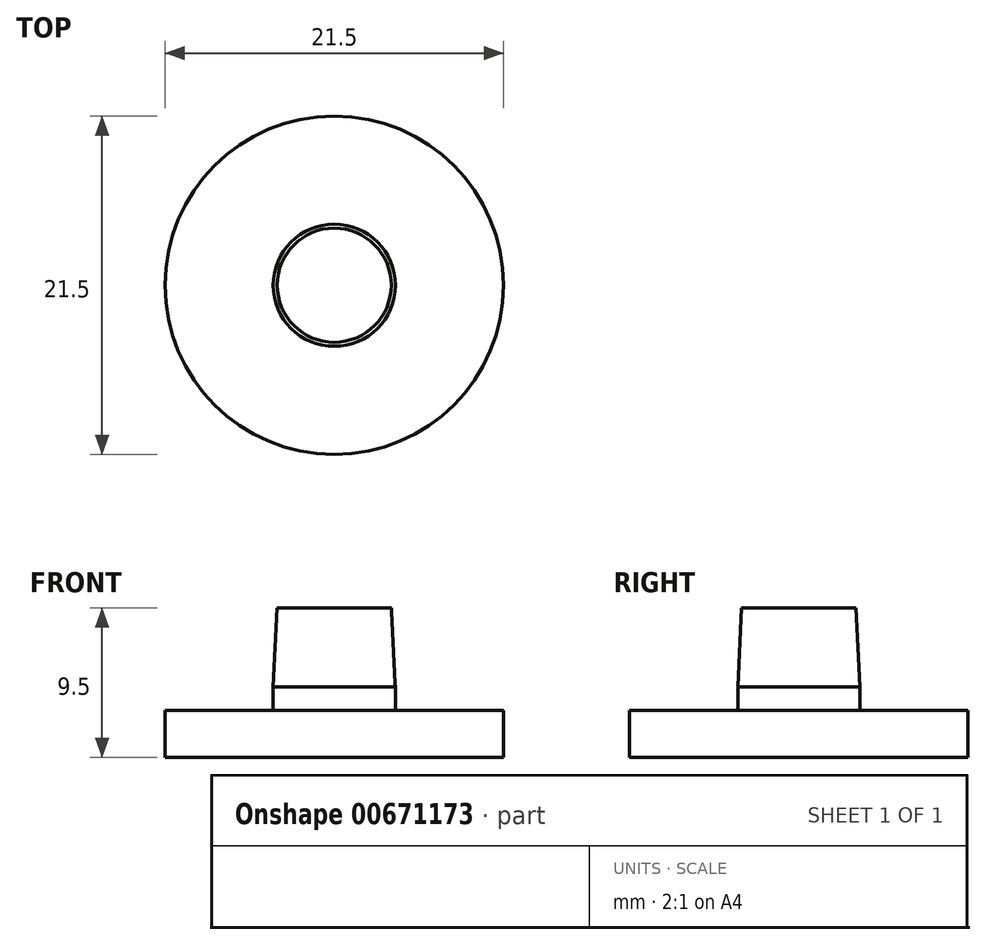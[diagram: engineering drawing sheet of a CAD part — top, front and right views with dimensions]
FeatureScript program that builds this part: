
annotation { "Feature Type Name" : "Feature", "Feature Type Description" : "" }
export const myFeature = defineFeature(function(context is Context, id is Id, definition is map)
    precondition{}
    {
        {
            var Q0;
            Q0=qCreatedBy(makeId("Top.planeOp"),FACE);
            var sketch = newSketch(context, id + "F0", { "sketchPlane" : qUnion([Q0])});
            skCircle(sketch, "E0", {"center": v(0, 0) * mm, "radius": 10.75 * mm});
            skSolve(sketch);
        }
        {
            var Q0;
            Q0 = qSketchRegion(id + "F0", true);
            extrude(context, id + "F1", {"entities" : qUnion([Q0]), "depth" : 3 * mm, "offsetDistance" : 25 * mm});
        }
        {
            var Q0;
            Q0=makeQuery(id+"F1.opExtrude","CAP_FACE",FACE,{"disambiguationData":[OSD([sQuery(id+"F0.wireOp",EDGE,"E0")])],"isStart":false});
            var sketch = newSketch(context, id + "F2", { "sketchPlane" : qUnion([Q0])});
            skCircle(sketch, "E1", {"center": v(0, 0) * mm, "radius": 3.88 * mm});
            skSolve(sketch);
        }
        {
            var Q0;
            Q0 = qSketchRegion(id + "F2", true);
            extrude(context, id + "F3", {"entities" : qUnion([Q0]), "operationType" : NewBodyOperationType.ADD, "depth" : 6.5 * mm, "offsetDistance" : 25 * mm});
        }
        {
            var Q0;
            Q0=makeQuery(id+"F3.opExtrude","CAP_EDGE",EDGE,{"disambiguationData":[OSD([sQuery(id+"F2.wireOp",EDGE,"E1")])],"isStart":false});
            chamfer(context, id + "F4", {"entities" : qUnion([Q0]), "chamferType" : ChamferType.TWO_OFFSETS, "width1" : .25 * mm, "oppositeDirection" : false, "width2" : 5 * mm, "tangentPropagation" : true});
        }
    });
